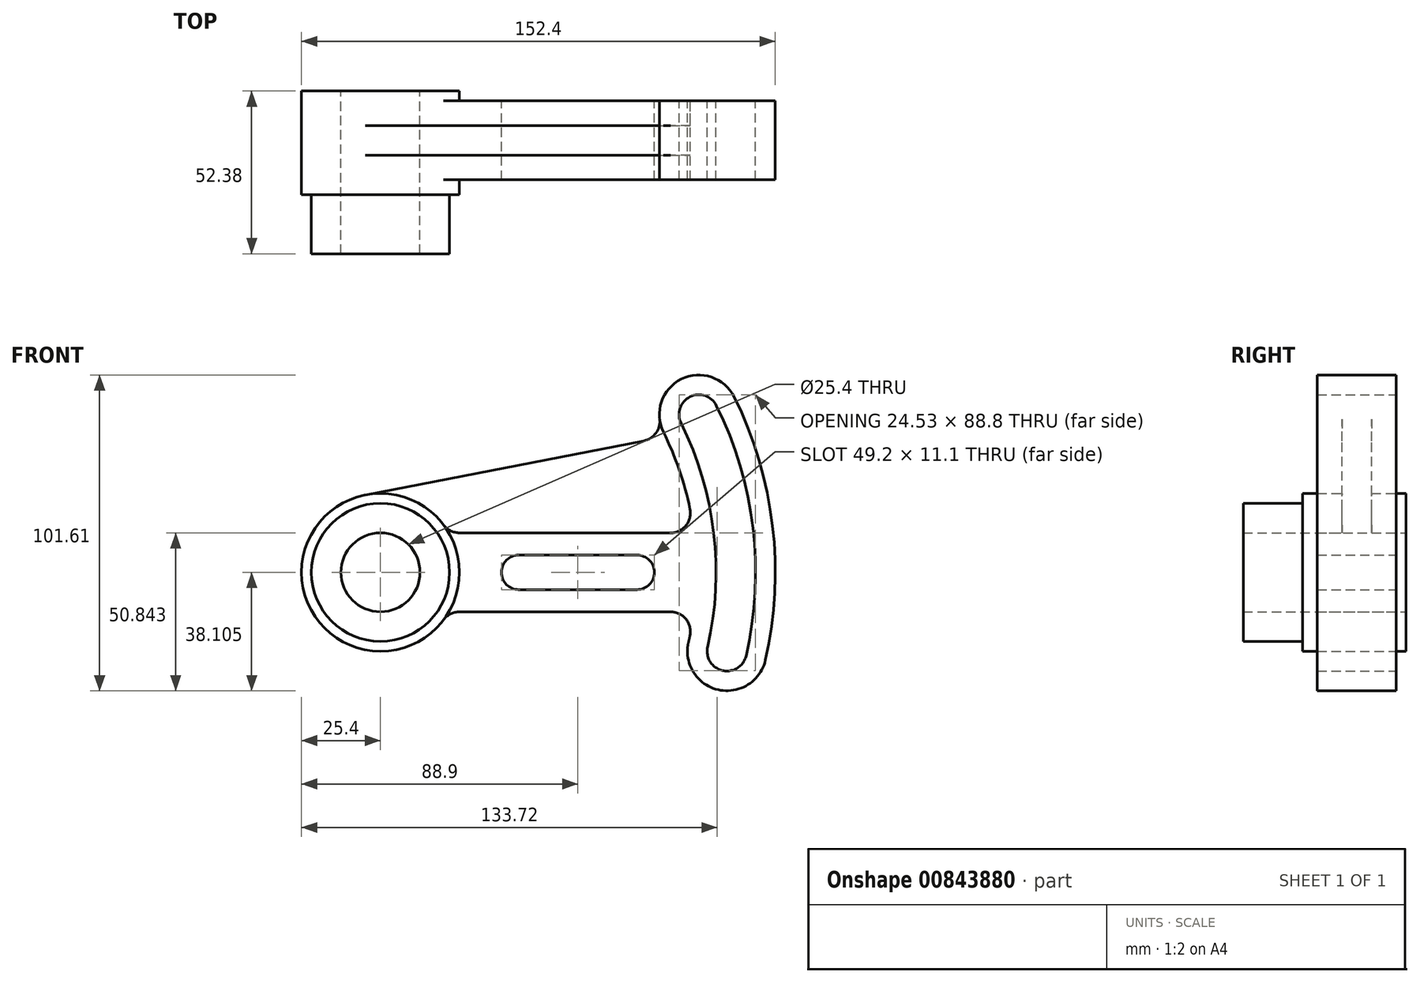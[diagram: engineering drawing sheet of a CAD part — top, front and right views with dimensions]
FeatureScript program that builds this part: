
annotation { "Feature Type Name" : "Feature", "Feature Type Description" : "" }
export const myFeature = defineFeature(function(context is Context, id is Id, definition is map)
    precondition{}
    {
        {
            var Q0;
            Q0=qCreatedBy(makeId("Top.planeOp"),FACE);
            var sketch = newSketch(context, id + "F0", { "sketchPlane" : qUnion([Q0])});
            skCircle(sketch, "E0", {"center": v(0, 0) * mm, "radius": 12.7 * mm});
            skArc(sketch, "E1", {"start": v(105.25, -23.99) * mm, "mid": v(110.03, -31.6) * mm, "end": v(117.63, -26.81) * mm});
            skArc(sketch, "E2", {"start": v(108.08, 53.62) * mm, "mid": v(99.57, 56.49) * mm, "end": v(96.7, 47.98) * mm});
            skArc(sketch, "E3", {"start": v(117.63, -26.81) * mm, "mid": v(119.8, 14.23) * mm, "end": v(108.08, 53.62) * mm});
            skArc(sketch, "E4", {"start": v(105.25, -23.99) * mm, "mid": v(107.2, 12.73) * mm, "end": v(96.7, 47.98) * mm});
            skArc(sketch, "E5", {"start": v(113.77, 56.44) * mm, "mid": v(96.75, 62.18) * mm, "end": v(91.01, 45.16) * mm});
            skArc(sketch, "E6", {"start": v(99.06, -22.58) * mm, "mid": v(108.62, -37.78) * mm, "end": v(123.82, -28.22) * mm});
            skArc(sketch, "E7", {"start": v(123.82, -28.22) * mm, "mid": v(126.11, 14.98) * mm, "end": v(113.77, 56.44) * mm});
            skArc(sketch, "E8", {"start": v(99.06, -22.58) * mm, "mid": v(99.3, -21.45) * mm, "end": v(99.55, -20.32) * mm});
            skLineSegment(sketch, "E9", {"start": v(57.15, 12.7) * mm, "end": v(93.33, 12.7) * mm});
            skLineSegment(sketch, "E10", {"start": v(54.68, -12.7) * mm, "end": v(93.33, -12.7) * mm});
            skArc(sketch, "E11.filletArc", {"start": v(93.33, 12.7) * mm, "mid": v(98.24, 15.03) * mm, "end": v(99.55, 20.32) * mm});
            skArc(sketch, "E12.filletArc", {"start": v(99.55, -20.32) * mm, "mid": v(98.24, -15.03) * mm, "end": v(93.33, -12.7) * mm});
            skArc(sketch, "E13.trimOffspring", {"start": v(99.55, 20.32) * mm, "mid": v(96.09, 33.01) * mm, "end": v(91.01, 45.16) * mm});
            skCircle(sketch, "E14", {"center": v(0, 0) * mm, "radius": 22.23 * mm});
            skLineSegment(sketch, "E15", {"start": v(57.15, 12.7) * mm, "end": v(25.4, 12.7) * mm});
            skLineSegment(sketch, "E16", {"start": v(54.68, -12.7) * mm, "end": v(25.4, -12.7) * mm});
            skPoint(sketch, "E17.start.orphan", {"position": v(57.15, 0) * mm});
            skArc(sketch, "E18", {"start": v(20.32, 15.24) * mm, "mid": v(-25.4, 0) * mm, "end": v(20.32, -15.24) * mm});
            skCircle(sketch, "E19", {"center": v(0, 0) * mm, "radius": 25.4 * mm});
            skPoint(sketch, "E20.visualSharp", {"position": v(22, 12.7) * mm});
            skArc(sketch, "E20.filletArc", {"start": v(20.32, 15.24) * mm, "mid": v(22.56, 13.37) * mm, "end": v(25.4, 12.7) * mm});
            skArc(sketch, "E21.filletArc", {"start": v(25.4, -12.7) * mm, "mid": v(22.56, -13.37) * mm, "end": v(20.32, -15.24) * mm});
            skPoint(sketch, "E22.orphan", {"position": v(114.3, 0) * mm});
            skArc(sketch, "E23", {"start": v(82.55, -5.55) * mm, "mid": v(88.1, 0) * mm, "end": v(82.55, 5.55) * mm});
            skArc(sketch, "E24", {"start": v(44.45, 5.55) * mm, "mid": v(38.9, 0) * mm, "end": v(44.45, -5.55) * mm});
            skLineSegment(sketch, "E25", {"start": v(44.45, 5.55) * mm, "end": v(82.55, 5.55) * mm});
            skLineSegment(sketch, "E26", {"start": v(44.45, -5.55) * mm, "end": v(82.55, -5.55) * mm});
            skLineSegment(sketch, "E27", {"start": v(-4.85, 24.93) * mm, "end": v(84.68, 42.34) * mm});
            skArc(sketch, "E28.filletArc", {"start": v(84.68, 42.34) * mm, "mid": v(88.6, 44.82) * mm, "end": v(89.78, 49.31) * mm});
            skSolve(sketch);
        }
        {
            var Q0;
            Q0=makeQuery(id+"F0.imprint","IMPRINT",FACE,{"disambiguationData":[TD([[makeQuery(id+"F0.imprint","IMPRINT",EDGE,{"derivedFrom":sQuery(id+"F0.wireOp",EDGE,"E14")}),-1.0]])]});
            extrude(context, id + "F1", {"entities" : qUnion([Q0]), "depth" : 33.32 * mm, "offsetDistance" : 25.4 * mm});
        }
        {
            var Q0;
            Q0=makeQuery(id+"F0.imprint","IMPRINT",FACE,{"disambiguationData":[TD([[makeQuery(id+"F0.imprint","IMPRINT",EDGE,{"derivedFrom":sQuery(id+"F0.wireOp",EDGE,"E0")}),-1.0]])]});
            extrude(context, id + "F2", {"entities" : qUnion([Q0]), "operationType" : NewBodyOperationType.ADD, "depth" : 52.37 * mm, "offsetDistance" : 25.4 * mm});
        }
        {
            var Q0;
            Q0=makeQuery(id+"F0.imprint","IMPRINT",FACE,{"disambiguationData":[TD([[makeQuery(id+"F0.imprint","IMPRINT",EDGE,{"derivedFrom":sQuery(id+"F0.wireOp",EDGE,"E1")}),-1.0]])]});
            extrude(context, id + "F3", {"entities" : qUnion([Q0]), "operationType" : NewBodyOperationType.ADD, "depth" : 28.57 * mm, "offsetDistance" : 25.4 * mm});
        }
        {
            var Q0;
            Q0=makeQuery(id+"F0.imprint","IMPRINT",FACE,{"disambiguationData":[TD([[makeQuery(id+"F0.imprint","IMPRINT",EDGE,{"derivedFrom":sQuery(id+"F0.wireOp",EDGE,"E9")}),1.0]])]});
            extrude(context, id + "F4", {"entities" : qUnion([Q0]), "operationType" : NewBodyOperationType.ADD, "depth" : 20.62 * mm, "offsetDistance" : 25.4 * mm});
        }
        {
            var Q0;
            Q0=makeQuery(id+"F0.imprint","IMPRINT",FACE,{"disambiguationData":[TD([[makeQuery(id+"F0.imprint","IMPRINT",EDGE,{"derivedFrom":sQuery(id+"F0.wireOp",EDGE,"E1")}),-1.0]])]});
            extrude(context, id + "F5", {"entities" : qUnion([Q0]), "operationType" : NewBodyOperationType.REMOVE, "depth" : 3.17 * mm, "offsetDistance" : 25.4 * mm});
        }
        {
            var Q0;
            Q0=makeQuery(id+"F0.imprint","IMPRINT",FACE,{"disambiguationData":[TD([[makeQuery(id+"F0.imprint","IMPRINT",EDGE,{"derivedFrom":sQuery(id+"F0.wireOp",EDGE,"E9")}),1.0]])]});
            extrude(context, id + "F6", {"entities" : qUnion([Q0]), "operationType" : NewBodyOperationType.REMOVE, "depth" : 11.1 * mm, "offsetDistance" : 25.4 * mm});
        }
        {
            var Q0;
            Q0=makeQuery(id+"F1.opExtrude","SWEPT_BODY",BODY,{"disambiguationData":[OSD([sQuery(id+"F0.wireOp",EDGE,"E14"),sQuery(id+"F0.wireOp",EDGE,"E19")])]});
            var Q1;
            Q1=qCreatedBy(makeId("Origin.pointOp"),VERTEX);
            var Q2;
            Q2=makeQuery(id+"F3.opExtrude","CAP_EDGE",EDGE,{"disambiguationData":[OSD([sQuery(id+"F0.wireOp",EDGE,"E9"),sQuery(id+"F0.wireOp",EDGE,"E15")])],"isStart":false});
            transform(context, id + "F7", {"entities" : qUnion([Q0]), "transformType" : TransformType.ROTATION, "transformAxis" : qUnion([Q2]), "angle" : 90 * degree, "makeCopy" : false});
        }
    });
